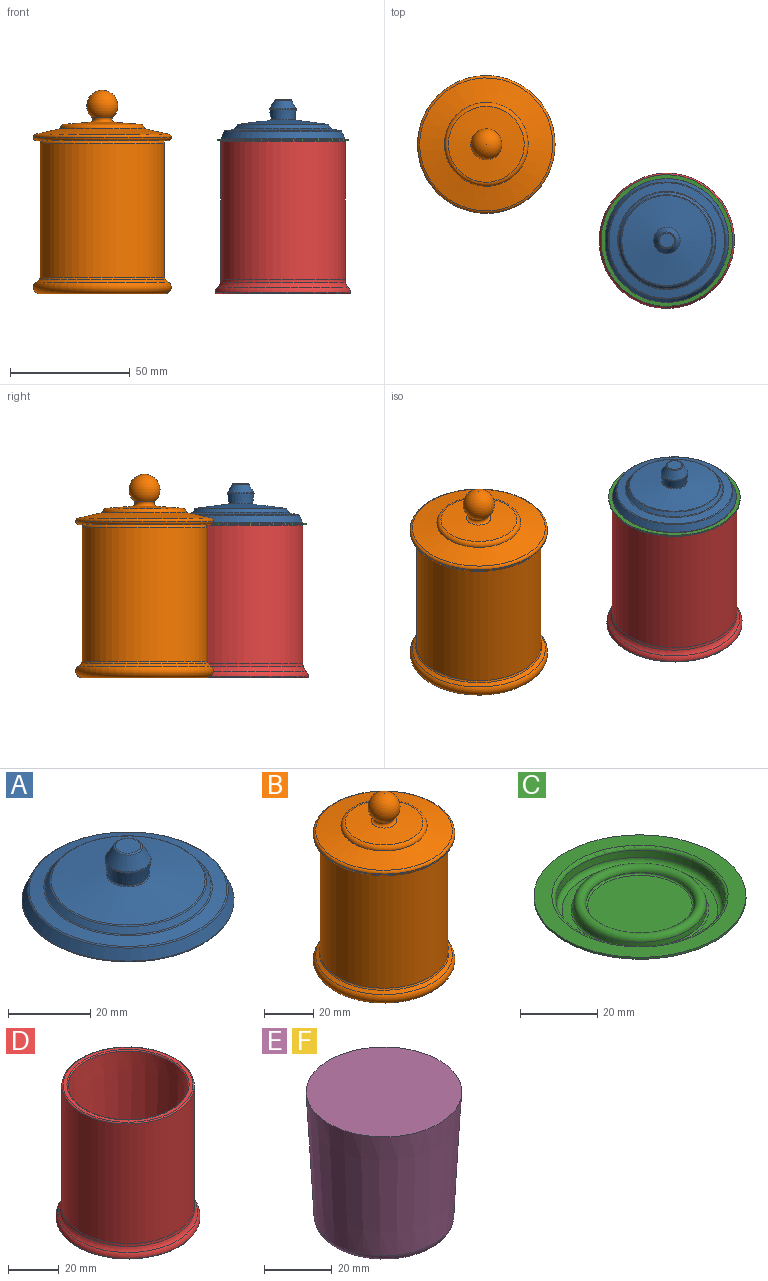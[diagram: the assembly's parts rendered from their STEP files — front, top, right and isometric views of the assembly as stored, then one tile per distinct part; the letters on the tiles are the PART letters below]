
ASSEMBLY  parts=6 mates=6
PART A: 22 faces, bbox 56x56x19.5 mm
  f0: torus R=3.11mm, axis (0,0,1), area 11.2mm2, adj f1,f21
  f1: plane 6.21x6.21mm, normal (0,0,1), area 30.3mm2, adj f0
  f2: sphere r=54mm, area 928mm2, adj f3
  f3: torus R=16.34mm, axis (0,0,1), area 272.7mm2, adj f2,f4
  f4: cone r=18.34mm half-angle=2deg, axis (0,0,-1), area 76.5mm2, adj f3,f5
  f5: torus R=19.36mm, axis (0,0,1), area 180.8mm2, adj f4,f6
  f6: plane 40.86x40.86mm, normal (0,0,-1), area 133.6mm2, adj f5,f7
  f7: torus R=20.43mm, axis (0,0,1), area 203.2mm2, adj f6,f8
  f8: cone r=21.5mm half-angle=2deg, axis (0,0,1), area 274.6mm2, adj f7,f9
  f9: plane 51.22x51.22mm, normal (0,0,-1), area 607.9mm2, adj f8,f10
  f10: torus R=25.61mm, axis (0,0,1), area 81.3mm2, adj f9,f11
  f11: cone r=25.83mm half-angle=25deg, axis (0,0,-1), area 507.7mm2, adj f10,f12
  f12: torus R=24.02mm, axis (0,0,1), area 72.5mm2, adj f11,f13
  f13: cone r=24.12mm half-angle=79.4deg, axis (0,0,-1), area 508mm2, adj f12,f14
  f14: torus R=20.65mm, axis (0,0,1), area 48.5mm2, adj f13,f15
  f15: cone r=20.25mm half-angle=36deg, axis (0,0,-1), area 235.6mm2, adj f14,f16
  f16: torus R=18.72mm, axis (0,0,1), area 48.2mm2, adj f15,f17
  f17: cone r=5.25mm half-angle=82.4deg, axis (0,0,-1), area 1031.5mm2, adj f16,f18
  f18: torus R=5.28mm, axis (0,0,1), area 12.6mm2, adj f17,f19
  f19: cone r=5.03mm half-angle=7.9deg, axis (0,0,1), area 137.8mm2, adj f18,f20
  f20: torus R=5.11mm, axis (0,0,1), area 11.3mm2, adj f19,f21
  f21: cone r=5.54mm half-angle=29.1deg, axis (0,0,-1), area 117.5mm2, adj f0,f20
PART B: 32 faces, bbox 62.2x62.2x85 mm
  f0: cylinder r=26mm len=56.02mm, axis (0,0,1), area 9151.1mm2, adj f1,f5
  f1: torus R=24.75mm, axis (0,0,1), area 315.2mm2, adj f0,f14
  f2: sphere r=339.8mm, area 2135mm2, adj f3
  f3: torus R=26.05mm, axis (0,0,1), area 1160.7mm2, adj f2,f4
  f4: cone r=26.36mm half-angle=50deg, axis (0,0,-1), area 317.1mm2, adj f3,f5
  f5: torus R=27mm, axis (0,0,1), area 143.2mm2, adj f0,f4
  f6: sphere r=6.5mm, area 461.7mm2, adj f7
  f7: torus R=5.19mm, axis (0,0,1), area 75.3mm2, adj f6,f8
  f8: cone r=15.84mm half-angle=85.6deg, axis (0,0,-1), area 708.4mm2, adj f7,f9
  f9: torus R=15.7mm, axis (0,0,1), area 285.7mm2, adj f8,f10
  f10: cone r=27.78mm half-angle=77.1deg, axis (0,0,-1), area 1500mm2, adj f9,f11
  f11: torus R=27.5mm, axis (0,0,1), area 300.2mm2, adj f10,f12
  f12: cylinder r=28.75mm len=57.5mm, axis (0,0,1), area 32mm2, adj f11,f13
  f13: torus R=27.5mm, axis (0,0,1), area 349.1mm2, adj f12,f14
  f14: plane 55x55mm, normal (0,0,-1), area 451.4mm2, adj f1,f13
  f15: plane 49.37x49.37mm, normal (0,0,-1), area 868.2mm2, adj f17,f31
  f16: plane 37x37mm, normal (0,0,1), area 28.9mm2, adj f17,f25
  f17: cylinder r=18.25mm len=36.5mm, axis (0,0,1), area 860mm2, adj f15,f16
  f18: plane 17.1x17.1mm, normal (0,0,-1), area 229.7mm2, adj f19
  f19: torus R=8.55mm, axis (0,0,1), area 732.5mm2, adj f18,f20
  f20: cylinder r=14.55mm len=29.1mm, axis (0,0,1), area 731.4mm2, adj f19,f21
  f21: torus R=15.55mm, axis (0,0,1), area 147.2mm2, adj f20,f22
  f22: plane 36.2x36.2mm, normal (0,0,-1), area 269.6mm2, adj f21,f23
  f23: torus R=18.1mm, axis (0,0,1), area 262.4mm2, adj f22,f24
  f24: cylinder r=19.5mm len=39mm, axis (0,0,1), area 12.3mm2, adj f23,f25
  f25: torus R=18.5mm, axis (0,0,1), area 188.9mm2, adj f16,f24
  f26: plane 16x16mm, normal (0,0,1), area 201.1mm2, adj f27
  f27: cone r=9mm half-angle=59deg, axis (0,0,1), area 62.3mm2, adj f26,f28
  f28: plane 36.28x36.28mm, normal (0,0,1), area 779.3mm2, adj f27,f29
  f29: torus R=18.14mm, axis (0,0,1), area 469.9mm2, adj f28,f30
  f30: cone r=23.44mm half-angle=3deg, axis (0,0,1), area 7410.6mm2, adj f29,f31
  f31: torus R=24.69mm, axis (0,0,1), area 285.1mm2, adj f15,f30
PART C: 23 faces, bbox 55x55x5 mm
  f0: plane 27.27x27.27mm, normal (0,0,-1), area 583.9mm2, adj f18
  f1: cone r=14.55mm half-angle=5deg, axis (0,0,1), area 16.1mm2, adj f2,f18
  f2: torus R=15.64mm, axis (0,0,-1), area 291.6mm2, adj f1,f3
  f3: cone r=16.64mm half-angle=5deg, axis (0,0,-1), area 165.9mm2, adj f2,f17
  f4: plane 40.56x40.56mm, normal (0,0,-1), area 300.2mm2, adj f15,f17
  f5: cone r=22.12mm half-angle=5deg, axis (0,0,1), area 298.8mm2, adj f15,f22
  f6: plane 55x55mm, normal (0,0,-1), area 720mm2, adj f7,f22
  f7: cylinder r=27.5mm len=55mm, axis (0,0,-1), area 103.7mm2, adj f6,f8
  f8: plane 55x55mm, normal (0,0,1), area 733.2mm2, adj f7,f21
  f9: cone r=21.95mm half-angle=5deg, axis (0,0,1), area 290.9mm2, adj f16,f21
  f10: plane 40.38x40.38mm, normal (0,0,1), area 278.3mm2, adj f16,f20
  f11: cone r=17.4mm half-angle=5deg, axis (0,0,-1), area 161.8mm2, adj f12,f20
  f12: torus R=15.64mm, axis (0,0,-1), area 466.5mm2, adj f11,f13
  f13: cone r=14mm half-angle=5deg, axis (0,0,1), area 7.4mm2, adj f12,f19
  f14: plane 27.08x27.08mm, normal (0,0,1), area 576.1mm2, adj f19
  f15: torus R=20.28mm, axis (0,0,-1), area 401.1mm2, adj f4,f5
  f16: torus R=20.19mm, axis (0,0,1), area 295.2mm2, adj f9,f10
  f17: torus R=17.77mm, axis (0,0,-1), area 159.9mm2, adj f3,f4
  f18: torus R=13.63mm, axis (0,0,-1), area 132.8mm2, adj f0,f1
  f19: torus R=13.54mm, axis (0,0,-1), area 64.5mm2, adj f13,f14
  f20: torus R=17.86mm, axis (0,0,1), area 81.8mm2, adj f10,f11
  f21: torus R=22.87mm, axis (0,0,1), area 207.4mm2, adj f8,f9
  f22: torus R=22.96mm, axis (0,0,-1), area 105.6mm2, adj f5,f6
PART D: 15 faces, bbox 65x65x64 mm
  f0: torus R=23.97mm, axis (0,0,1), area 112.9mm2, adj f1,f14
  f1: cone r=23.48mm half-angle=3deg, axis (0,0,1), area 7515.5mm2, adj f0,f2
  f2: torus R=18.14mm, axis (0,0,1), area 469.9mm2, adj f1,f3
  f3: plane 36.28x36.28mm, normal (0,0,1), area 1033.8mm2, adj f2
  f4: plane 42.5x42.5mm, normal (0,0,-1), area 1418.6mm2, adj f5
  f5: torus R=21.25mm, axis (0,0,1), area 216mm2, adj f4,f6
  f6: torus R=23.25mm, axis (0,0,1), area 223.2mm2, adj f5,f7
  f7: plane 55.5x55.5mm, normal (0,0,-1), area 721mm2, adj f6,f8
  f8: torus R=27.75mm, axis (0,0,1), area 138.5mm2, adj f7,f9
  f9: torus R=25.25mm, axis (0,0,1), area 430.2mm2, adj f8,f10
  f10: torus R=30.04mm, axis (0,0,1), area 413.5mm2, adj f9,f11
  f11: torus R=32mm, axis (0,0,1), area 195.1mm2, adj f10,f12
  f12: cylinder r=26mm len=57.5mm, axis (0,0,1), area 9393.4mm2, adj f11,f13
  f13: torus R=25.5mm, axis (0,0,1), area 127.4mm2, adj f12,f14
  f14: plane 51x51mm, normal (0,0,1), area 237.1mm2, adj f0,f13
PART E: 4 faces, bbox 46x46x47 mm
  f0: plane 45.95x45.95mm, normal (0,0,1), area 1658.4mm2, adj f3
  f1: plane 36.28x36.28mm, normal (0,0,-1), area 1033.8mm2, adj f2
  f2: torus R=18.14mm, axis (0,0,-1), area 469.9mm2, adj f1,f3
  f3: cone r=22.98mm half-angle=3deg, axis (0,0,1), area 6123.4mm2, adj f0,f2
PART F: same geometry as E
PLACE A t=(13.64,-20.55,22.97)mm
PLACE B rot(axis=(0,0,-1),20.6deg) t=(-61.81,19.63,22.37)mm fixed
PLACE C t=(13.64,-20.55,81.97)mm
PLACE D t=(13.64,-20.55,22.37)mm fixed
PLACE E t=(13.64,-20.55,22.37)mm fixed
PLACE F rot(axis=(0,0,1),34.5deg) t=(-61.81,19.63,22.24)mm
MATE cylindrical C.f1 <-> E.f2  axis (0,0,1) through (13.64,-20.55,83.97)mm
MATE planar D.f0 <-> C.f1  axis (0,0,1) through (13.64,-20.55,86.37)mm
MATE planar B.f0 <-> D.f11  axis (0,0,1) through (-61.81,19.63,22.37)mm
MATE planar C.f1 <-> A.f18  axis (0,0,1) through (13.64,-20.55,86.97)mm
MATE cylindrical A.f8 <-> D.f12  axis (0,0,1) through (13.64,-20.55,99.3)mm
MATE cylindrical B.f27 <-> F.f3  axis (0,0,1) through (-61.81,19.63,57.11)mm
